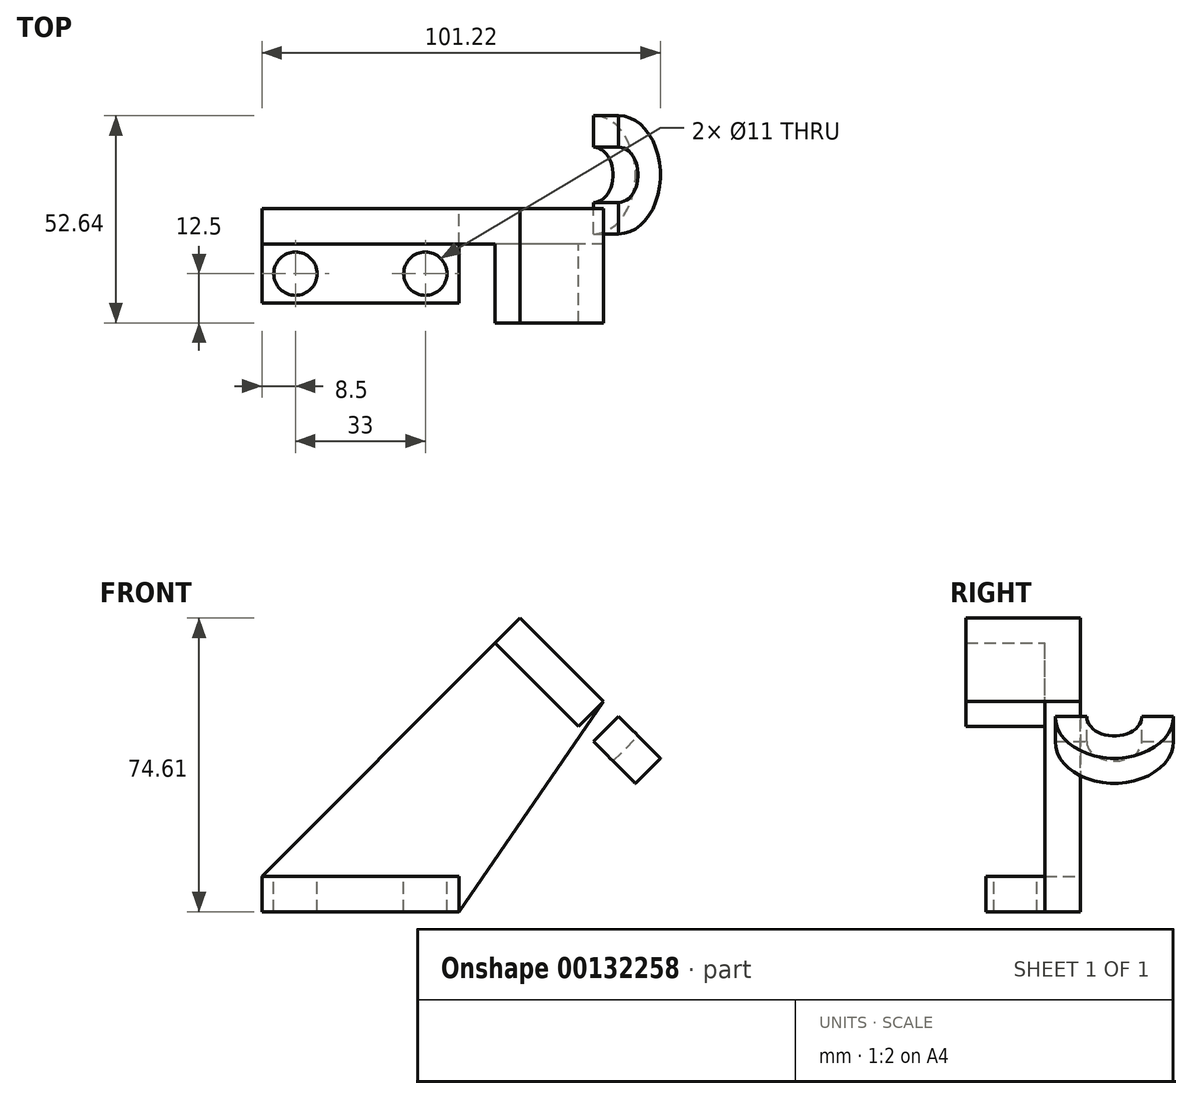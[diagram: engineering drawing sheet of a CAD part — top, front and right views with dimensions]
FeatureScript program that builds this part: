
annotation { "Feature Type Name" : "Feature", "Feature Type Description" : "" }
export const myFeature = defineFeature(function(context is Context, id is Id, definition is map)
    precondition{}
    {
        {
            var Q0;
            Q0=qCreatedBy(makeId("Front.planeOp"),FACE);
            var sketch = newSketch(context, id + "F0", { "sketchPlane" : qUnion([Q0])});
            skLineSegment(sketch, "E0.bottom", {"start": v(0, 0) * mm, "end": v(50, 0) * mm});
            skLineSegment(sketch, "E0.top", {"start": v(0, 9) * mm, "end": v(50, 9) * mm});
            skLineSegment(sketch, "E0.left", {"start": v(0, 0) * mm, "end": v(0, 9) * mm});
            skLineSegment(sketch, "E0.right", {"start": v(50, 0) * mm, "end": v(50, 9) * mm});
            skLineSegment(sketch, "E1", {"start": v(0, 9) * mm, "end": v(65.6, 74.6) * mm});
            skLineSegment(sketch, "E2", {"start": v(65.6, 74.6) * mm, "end": v(86.82, 53.4) * mm});
            skLineSegment(sketch, "E3", {"start": v(86.82, 53.4) * mm, "end": v(80.46, 47.03) * mm});
            skLineSegment(sketch, "E4", {"start": v(80.46, 47.03) * mm, "end": v(59.24, 68.24) * mm});
            skLineSegment(sketch, "E5", {"start": v(86.82, 53.4) * mm, "end": v(50, 0) * mm});
            skLineSegment(sketch, "E6", {"start": v(76.21, 64) * mm, "end": v(105.31, 64) * mm, "construction": true});
            skLineSegment(sketch, "E7", {"start": v(50, 0) * mm, "end": v(91.35, 0) * mm, "construction": true});
            skSolve(sketch);
        }
        {
            var Q0;
            {var subQ1=sQuery(id+"F0.wireOp",EDGE,"E0.top");Q0=makeQuery(id+"F0.imprint","IMPRINT",FACE,{"disambiguationData":[TD([[makeQuery(id+"F0.imprint","IMPRINT",EDGE,{"derivedFrom":subQ1}),1.0]])]});}
            extrude(context, id + "F1", {"entities" : qUnion([Q0]), "depth" : 9 * mm});
        }
        {
            var Q0;
            {var subQ0=sQuery(id+"F0.wireOp",EDGE,"E2");Q0=makeQuery(id+"F0.imprint","IMPRINT",FACE,{"disambiguationData":[TD([[makeQuery(id+"F0.imprint","IMPRINT",EDGE,{"derivedFrom":subQ0}),-1.0]])]});}
            extrude(context, id + "F2", {"entities" : qUnion([Q0]), "operationType" : NewBodyOperationType.ADD, "depth" : 29 * mm});
        }
        {
            var Q0;
            Q0=makeQuery(id+"F2.opExtrude","SWEPT_FACE",FACE,{"disambiguationData":[OSD([sQuery(id+"F0.wireOp",EDGE,"E2")])]});
            var sketch = newSketch(context, id + "F3", { "sketchPlane" : qUnion([Q0])});
            skCircle(sketch, "E8", {"center": v(8.64, -29) * mm, "radius": 7 * mm});
            skLineSegment(sketch, "E9.bottom", {"start": v(-6.36, -29) * mm, "end": v(1.64, -29) * mm});
            skLineSegment(sketch, "E9.top", {"start": v(-6.36, 0) * mm, "end": v(23.64, 0) * mm});
            skLineSegment(sketch, "E9.left", {"start": v(-6.36, -29) * mm, "end": v(-6.36, 0) * mm});
            skLineSegment(sketch, "E9.right", {"start": v(23.64, -29) * mm, "end": v(23.64, 0) * mm});
            skLineSegment(sketch, "E10.trimOffspring", {"start": v(15.64, -29) * mm, "end": v(23.64, -29) * mm});
            skArc(sketch, "E11", {"start": v(-6.36, -29) * mm, "mid": v(8.64, -44) * mm, "end": v(23.64, -29) * mm});
            skSolve(sketch);
        }
        {
            var Q0;
            {var subQ0=sQuery(id+"F3.wireOp",EDGE,"E9.bottom");Q0=makeQuery(id+"F3.imprint","IMPRINT",FACE,{"disambiguationData":[TD([[makeQuery(id+"F3.imprint","IMPRINT",EDGE,{"derivedFrom":subQ0}),-1.0]])]});}
            extrude(context, id + "F4", {"entities" : qUnion([Q0]), "operationType" : NewBodyOperationType.ADD, "oppositeDirection" : true, "depth" : 9 * mm});
        }
        {
            var Q0;
            {var subQ0=sQuery(id+"F3.wireOp",EDGE,"E8");var subQ1=makeQuery(id+"F2.opExtrude","CAP_EDGE",EDGE,{"disambiguationData":[OSD([sQuery(id+"F0.wireOp",EDGE,"E2")])],"isStart":false});var subQ2=makeQuery(id+"F3.imprint","INTERSECT",VERTEX,{"derivedFrom":[subQ1,subQ0,sQuery(id+"F3.wireOp",EDGE,"E9.bottom")]});Q0=makeQuery(id+"F3.imprint","IMPRINT",FACE,{"disambiguationData":[TD([[makeQuery(id+"F3.imprint","IMPRINT",EDGE,{"disambiguationData":[TD([[subQ2,1.0]])],"derivedFrom":subQ0}),1.0]])]});}
            extrude(context, id + "F5", {"entities" : qUnion([Q0]), "operationType" : NewBodyOperationType.REMOVE, "oppositeDirection" : true, "depth" : 9 * mm});
        }
        {
            var Q0;
            Q0=makeQuery(id+"F0.imprint","IMPRINT",FACE,{"disambiguationData":[TD([[makeQuery(id+"F0.imprint","IMPRINT",EDGE,{"derivedFrom":sQuery(id+"F0.wireOp",EDGE,"E0.bottom")}),1.0]])]});
            extrude(context, id + "F6", {"entities" : qUnion([Q0]), "operationType" : NewBodyOperationType.ADD, "depth" : 24 * mm});
        }
        {
            var Q0;
            Q0=makeQuery(id+"F6.opExtrude","SWEPT_FACE",FACE,{"disambiguationData":[OSD([sQuery(id+"F0.wireOp",EDGE,"E0.top")])]});
            var sketch = newSketch(context, id + "F7", { "sketchPlane" : qUnion([Q0])});
            skLineSegment(sketch, "E12.bottom", {"start": v(0, -24) * mm, "end": v(50, -24) * mm});
            skLineSegment(sketch, "E12.top", {"start": v(0, -9) * mm, "end": v(50, -9) * mm});
            skLineSegment(sketch, "E12.left", {"start": v(0, -24) * mm, "end": v(0, -9) * mm});
            skLineSegment(sketch, "E12.right", {"start": v(50, -24) * mm, "end": v(50, -9) * mm});
            skCircle(sketch, "E13", {"center": v(8.5, -16.5) * mm, "radius": 5.5 * mm});
            skPoint(sketch, "E13.centerSnap0", {"position": v(0, -16.5) * mm});
            skCircle(sketch, "E14", {"center": v(41.5, -16.5) * mm, "radius": 5.5 * mm});
            skLineSegment(sketch, "E15", {"start": v(41.5, -16.5) * mm, "end": v(50, -16.5) * mm, "construction": true});
            skLineSegment(sketch, "E16", {"start": v(8.5, -16.5) * mm, "end": v(0, -16.5) * mm, "construction": true});
            skSolve(sketch);
        }
        {
            var Q0;
            Q0=makeQuery(id+"F7.imprint","IMPRINT",FACE,{"disambiguationData":[TD([[makeQuery(id+"F7.imprint","IMPRINT",EDGE,{"derivedFrom":sQuery(id+"F7.wireOp",EDGE,"E13")}),1.0]])]});
            var Q1;
            Q1=makeQuery(id+"F7.imprint","IMPRINT",FACE,{"disambiguationData":[TD([[makeQuery(id+"F7.imprint","IMPRINT",EDGE,{"derivedFrom":sQuery(id+"F7.wireOp",EDGE,"E14")}),1.0]])]});
            var Q2;
            Q2=sQuery(id+"F7.wireOp",EDGE,"E14");
            var Q3;
            Q3=sQuery(id+"F7.wireOp",EDGE,"E13");
            extrude(context, id + "F8", {"entities" : qUnion([Q0, Q1]), "operationType" : NewBodyOperationType.REMOVE, "surfaceEntities" : qUnion([Q2, Q3]), "endBound" : BoundingType.THROUGH_ALL, "oppositeDirection" : true, "depth" : 9 * mm});
        }
    });
